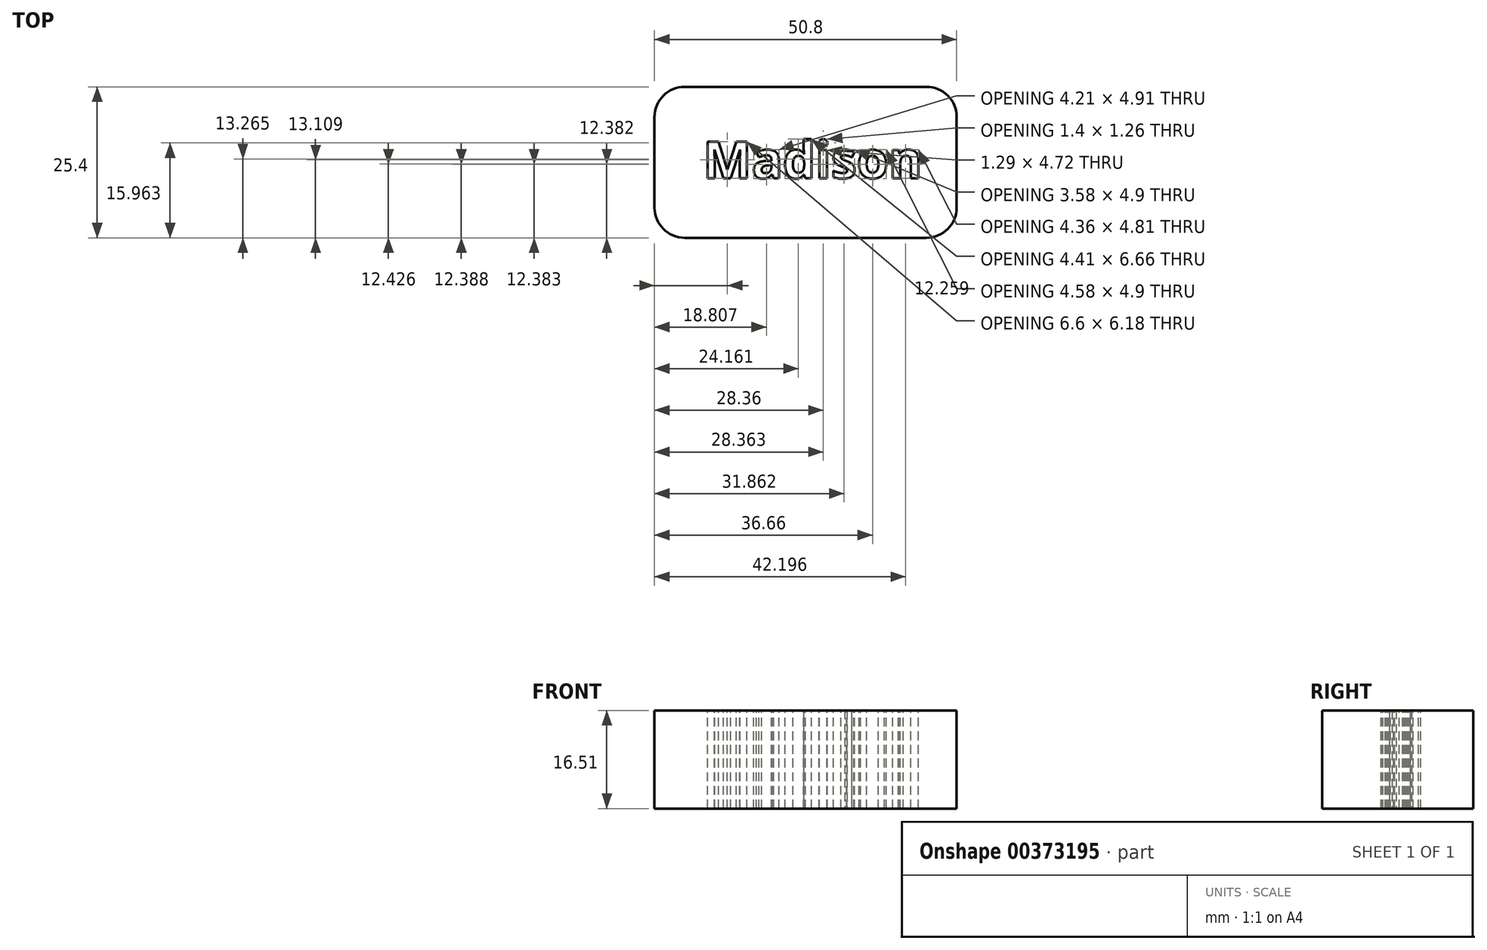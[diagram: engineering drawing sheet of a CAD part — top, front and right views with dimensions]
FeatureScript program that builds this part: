
annotation { "Feature Type Name" : "Feature", "Feature Type Description" : "" }
export const myFeature = defineFeature(function(context is Context, id is Id, definition is map)
    precondition{}
    {
        {
            var Q0;
            Q0=qCreatedBy(makeId("Front.planeOp"),FACE);
            var sketch = newSketch(context, id + "F0", { "sketchPlane" : qUnion([Q0])});
            skLineSegment(sketch, "E0", {"start": v(0, 16.5) * mm, "end": v(50.8, 16.5) * mm});
            skLineSegment(sketch, "E1", {"start": v(50.8, 16.5) * mm, "end": v(50.8, 0) * mm});
            skLineSegment(sketch, "E2", {"start": v(50.8, 0) * mm, "end": v(0, 0) * mm});
            skLineSegment(sketch, "E3", {"start": v(0, 0) * mm, "end": v(0, 16.5) * mm});
            skSolve(sketch);
        }
        {
            var Q0;
            Q0=makeQuery(id+"F0.imprint","IMPRINT",FACE,{"disambiguationData":[TD([[makeQuery(id+"F0.imprint","IMPRINT",EDGE,{"derivedFrom":sQuery(id+"F0.wireOp",EDGE,"E0")}),-1.0]])]});
            extrude(context, id + "F1", {"entities" : qUnion([Q0]), "depth" : 25.4 * mm});
        }
        {
            var Q0;
            Q0=makeQuery(id+"F1.opExtrude","SWEPT_FACE",FACE,{"disambiguationData":[OSD([sQuery(id+"F0.wireOp",EDGE,"E0")])]});
            var sketch = newSketch(context, id + "F2", { "sketchPlane" : qUnion([Q0])});
            skText(sketch, "E4", { "text": "Madison\n", "fontName": "OpenSans-Bold.ttf"});
            const initialGuessF2  = {"E4": [0.00818, -0.01538, 1, 0, 0.00623]};
            skSetInitialGuess(sketch, initialGuessF2);
            skSolve(sketch);
        }
        {
            var Q0;
            Q0 = qSketchRegion(id + "F2", true);
            extrude(context, id + "F3", {"entities" : qUnion([Q0]), "operationType" : NewBodyOperationType.REMOVE, "oppositeDirection" : true, "depth" : 25.4 * mm});
        }
        {
            var Q0;
            Q0=makeQuery(id+"F1.opExtrude","CAP_EDGE",EDGE,{"disambiguationData":[OSD([sQuery(id+"F0.wireOp",EDGE,"E3")])],"isStart":false});
            var Q1;
            Q1=makeQuery(id+"F1.opExtrude","CAP_EDGE",EDGE,{"disambiguationData":[OSD([sQuery(id+"F0.wireOp",EDGE,"E1")])],"isStart":false});
            var Q2;
            Q2=makeQuery(id+"F1.opExtrude","CAP_EDGE",EDGE,{"disambiguationData":[OSD([sQuery(id+"F0.wireOp",EDGE,"E1")])],"isStart":true});
            var Q3;
            Q3=makeQuery(id+"F1.opExtrude","CAP_EDGE",EDGE,{"disambiguationData":[OSD([sQuery(id+"F0.wireOp",EDGE,"E3")])],"isStart":true});
            fillet(context, id + "F4", {"entities" : qUnion([Q0, Q1, Q2, Q3]), "radius" : 5.08 * mm, "tangentPropagation" : true, "allowEdgeOverflow" : false});
        }
    });
